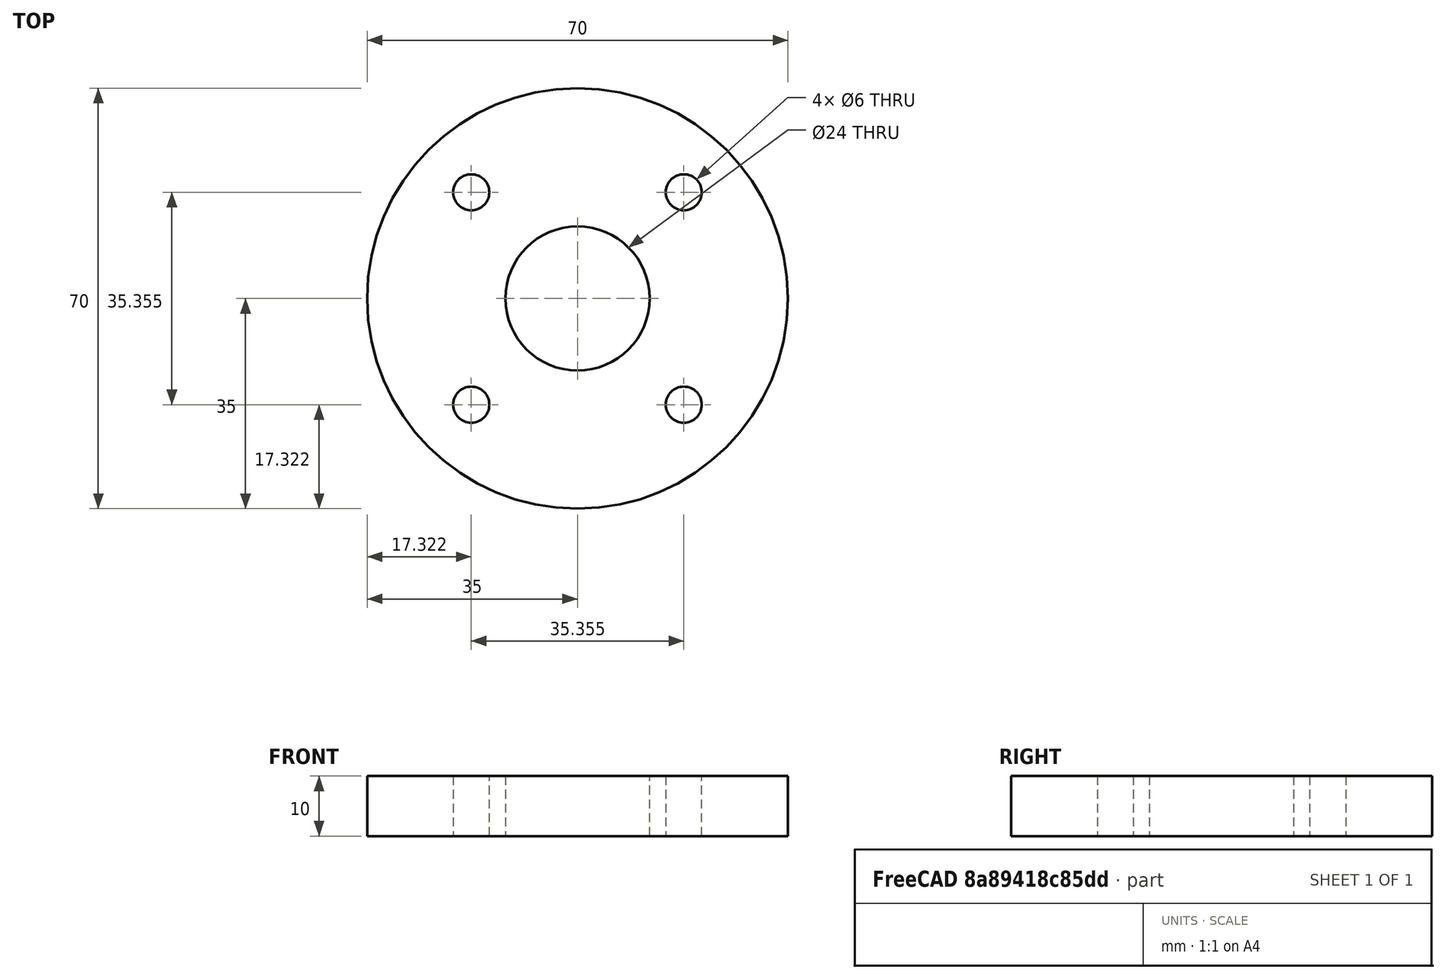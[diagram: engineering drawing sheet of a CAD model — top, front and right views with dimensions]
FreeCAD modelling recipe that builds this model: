
FCSTD DOCUMENT  (FreeCAD 0.19R24276 (Git))
Label: bldc_holder_p2_b_holder
License: All rights reserved
LicenseURL: http://en.wikipedia.org/wiki/All_rights_reserved
objects: Sketcher::SketchObject×1, PartDesign::Pad×1, PartDesign::Body×1
note: 4 computed .brp shape members not serialized (recipe doc carries the construction recipe); baked Part::Feature solids carry a one-line shape summary decoded from their .brp

FEATURE [Sketcher::SketchObject] Sketch
  FullyConstrained = true
  MapMode = 5
  Support = -> [XY_Plane]
  sketch-geometry (11):
    g0: Circle CenterX=0 CenterY=0 CenterZ=0 NormalX=0 NormalY=0 NormalZ=1 AngleXU=0 Radius=12
    g1: LineSegment StartX=17.6777 StartY=17.6777 StartZ=0 EndX=-17.6777 EndY=17.6777 EndZ=0
    g2: LineSegment StartX=-17.6777 StartY=17.6777 StartZ=0 EndX=-17.6777 EndY=-17.6777 EndZ=0
    g3: LineSegment StartX=-17.6777 StartY=-17.6777 StartZ=0 EndX=17.6777 EndY=-17.6777 EndZ=0
    g4: LineSegment StartX=17.6777 StartY=-17.6777 StartZ=0 EndX=17.6777 EndY=17.6777 EndZ=0
    g5: Circle CenterX=0 CenterY=0 CenterZ=0 NormalX=0 NormalY=0 NormalZ=1 AngleXU=0 Radius=25
    g6: Circle CenterX=-17.6777 CenterY=17.6777 CenterZ=0 NormalX=0 NormalY=0 NormalZ=1 AngleXU=0 Radius=3
    g7: Circle CenterX=17.6777 CenterY=17.6777 CenterZ=0 NormalX=0 NormalY=0 NormalZ=1 AngleXU=0 Radius=3
    g8: Circle CenterX=-17.6777 CenterY=-17.6777 CenterZ=0 NormalX=0 NormalY=0 NormalZ=1 AngleXU=0 Radius=3
    g9: Circle CenterX=17.6777 CenterY=-17.6777 CenterZ=0 NormalX=0 NormalY=0 NormalZ=1 AngleXU=0 Radius=3
    g10: Circle CenterX=0 CenterY=0 CenterZ=0 NormalX=0 NormalY=0 NormalZ=1 AngleXU=0 Radius=35
  constraints (26):
    c: Diameter(g0) = 24
    c: Coincident(g1,g2)
    c: Coincident(g2,g3)
    c: Coincident(g3,g4)
    c: Coincident(g4,g1)
    c: Equal(g1,g2)
    c: Equal(g1,g3)
    c: Equal(g1,g4)
    c: PointOnObject(g1,g5)
    c: PointOnObject(g2,g5)
    c: PointOnObject(g3,g5)
    c: PointOnObject(g4,g5)
    c: Coincident(g5,g0)
    c: Horizontal(g1)
    c: Diameter(g5) = 50
    c: Coincident(g6,g1)
    c: Coincident(g7,g1)
    c: Coincident(g8,g2)
    c: Coincident(g9,g3)
    c: Diameter(g6) = 6
    c: Equal(g6,g8)
    c: Equal(g6,g7)
    c: Equal(g6,g9)
    c: Coincident(g0,g-1)
    c: Coincident(g10,g0)
    c: Diameter(g10) = 70
FEATURE [PartDesign::Pad] Pad
  Direction = (1,1,1)
  Length = 10
  Length2 = 100
  Profile = -> Sketch
  Type = 0
FEATURE [PartDesign::Body] Body
  Group = -> [Sketch,Pad]
  Origin = -> Origin
  Tip = -> Pad
